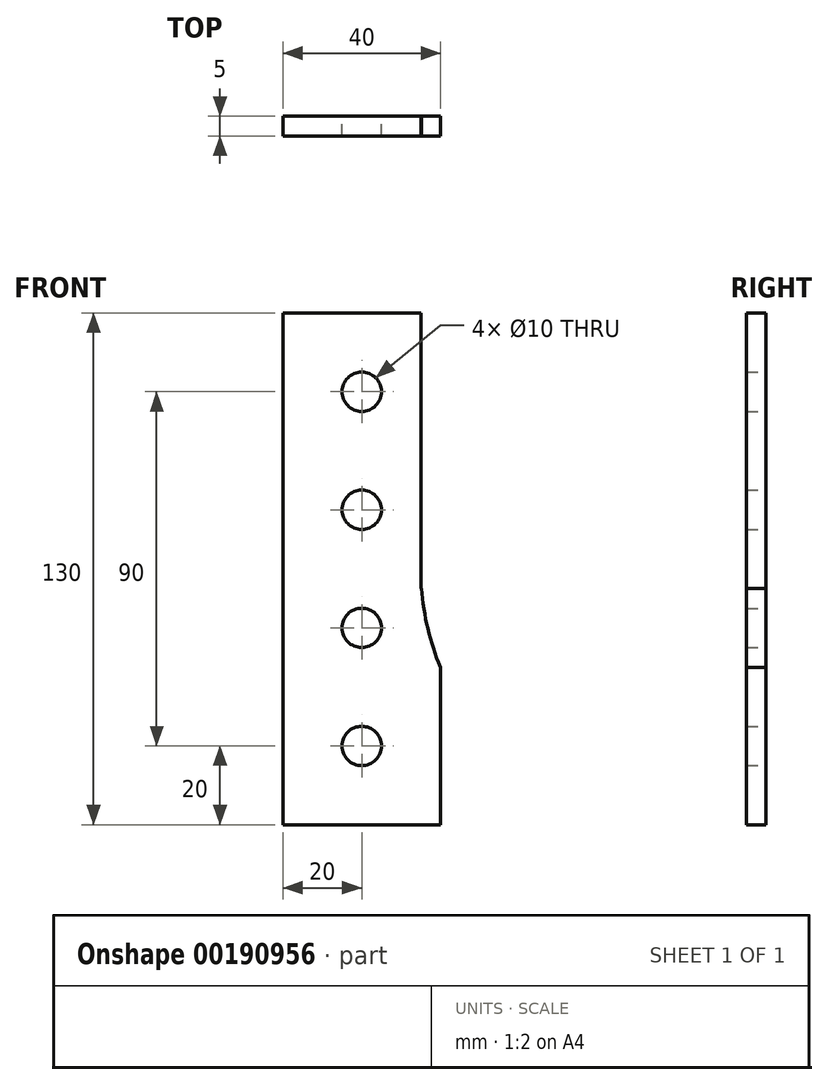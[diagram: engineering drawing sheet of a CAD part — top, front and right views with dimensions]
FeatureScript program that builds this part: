
annotation { "Feature Type Name" : "Feature", "Feature Type Description" : "" }
export const myFeature = defineFeature(function(context is Context, id is Id, definition is map)
    precondition{}
    {
        {
            var Q0;
            Q0=qCreatedBy(makeId("Front.planeOp"),FACE);
            var sketch = newSketch(context, id + "F0", { "sketchPlane" : qUnion([Q0])});
            skLineSegment(sketch, "E0.bottom", {"start": v(0, 0) * mm, "end": v(35, 0) * mm});
            skLineSegment(sketch, "E0.top", {"start": v(0, 130) * mm, "end": v(35, 130) * mm});
            skLineSegment(sketch, "E0.left", {"start": v(0, 0) * mm, "end": v(0, 130) * mm});
            skLineSegment(sketch, "E0.right", {"start": v(35, 0) * mm, "end": v(35, 130) * mm});
            skCircle(sketch, "E1", {"center": v(20, 110) * mm, "radius": 5 * mm});
            skCircle(sketch, "E2", {"center": v(20, 80) * mm, "radius": 5 * mm});
            skCircle(sketch, "E3", {"center": v(20, 50) * mm, "radius": 5 * mm});
            skCircle(sketch, "E4", {"center": v(20, 20) * mm, "radius": 5 * mm});
            skLineSegment(sketch, "E5.bottom", {"start": v(35, 60) * mm, "end": v(80, 60) * mm});
            skLineSegment(sketch, "E5.top", {"start": v(35, 70) * mm, "end": v(80, 70) * mm});
            skLineSegment(sketch, "E5.left", {"start": v(35, 60) * mm, "end": v(35, 70) * mm});
            skLineSegment(sketch, "E5.right", {"start": v(80, 60) * mm, "end": v(80, 70) * mm});
            skArc(sketch, "E6", {"start": v(80, 70) * mm, "mid": v(46.03, 88.11) * mm, "end": v(35, 125) * mm});
            skArc(sketch, "E7", {"start": v(75.5, 60) * mm, "mid": v(75, 65.31) * mm, "end": v(75.64, 70.6) * mm});
            skLineSegment(sketch, "E8.bottom", {"start": v(35, 0) * mm, "end": v(40, 0) * mm});
            skLineSegment(sketch, "E8.top", {"start": v(35, 60) * mm, "end": v(40, 60) * mm});
            skLineSegment(sketch, "E8.left", {"start": v(35, 0) * mm, "end": v(35, 60) * mm});
            skLineSegment(sketch, "E8.right", {"start": v(40, 0) * mm, "end": v(40, 60) * mm});
            skArc(sketch, "E9", {"start": v(40, 40) * mm, "mid": v(36.8, 49.8) * mm, "end": v(35.2, 60) * mm});
            skSolve(sketch);
        }
        {
            var Q0;
            {var subQ0=sQuery(id+"F0.wireOp",EDGE,"E0.bottom");Q0=makeQuery(id+"F0.imprint","IMPRINT",FACE,{"disambiguationData":[TD([[makeQuery(id+"F0.imprint","IMPRINT",EDGE,{"derivedFrom":subQ0}),1.0]])]});}
            var Q1;
            {var subQ1=sQuery(id+"F0.wireOp",EDGE,"E0.right");var subQ3=sQuery(id+"F0.wireOp",EDGE,"E6");var subQ4=makeQuery(id+"F0.imprint","INTERSECT",VERTEX,{"derivedFrom":[subQ1,subQ3]});Q1=makeQuery(id+"F0.imprint","IMPRINT",FACE,{"disambiguationData":[TD([[makeQuery(id+"F0.imprint","IMPRINT",EDGE,{"disambiguationData":[TD([[subQ4,1.0]])],"derivedFrom":subQ3}),1.0]])]});}
            var Q2;
            {var subQ0=sQuery(id+"F0.wireOp",EDGE,"E5.left");Q2=makeQuery(id+"F0.imprint","IMPRINT",FACE,{"disambiguationData":[TD([[makeQuery(id+"F0.imprint","IMPRINT",EDGE,{"derivedFrom":subQ0}),-1.0]])]});}
            var Q3;
            {var subQ1=sQuery(id+"F0.wireOp",EDGE,"E8.bottom");Q3=makeQuery(id+"F0.imprint","IMPRINT",FACE,{"disambiguationData":[TD([[makeQuery(id+"F0.imprint","IMPRINT",EDGE,{"derivedFrom":subQ1}),1.0]])]});}
            extrude(context, id + "F1", {"entities" : qUnion([Q0, Q1, Q2, Q3]), "depth" : 5 * mm});
        }
    });
